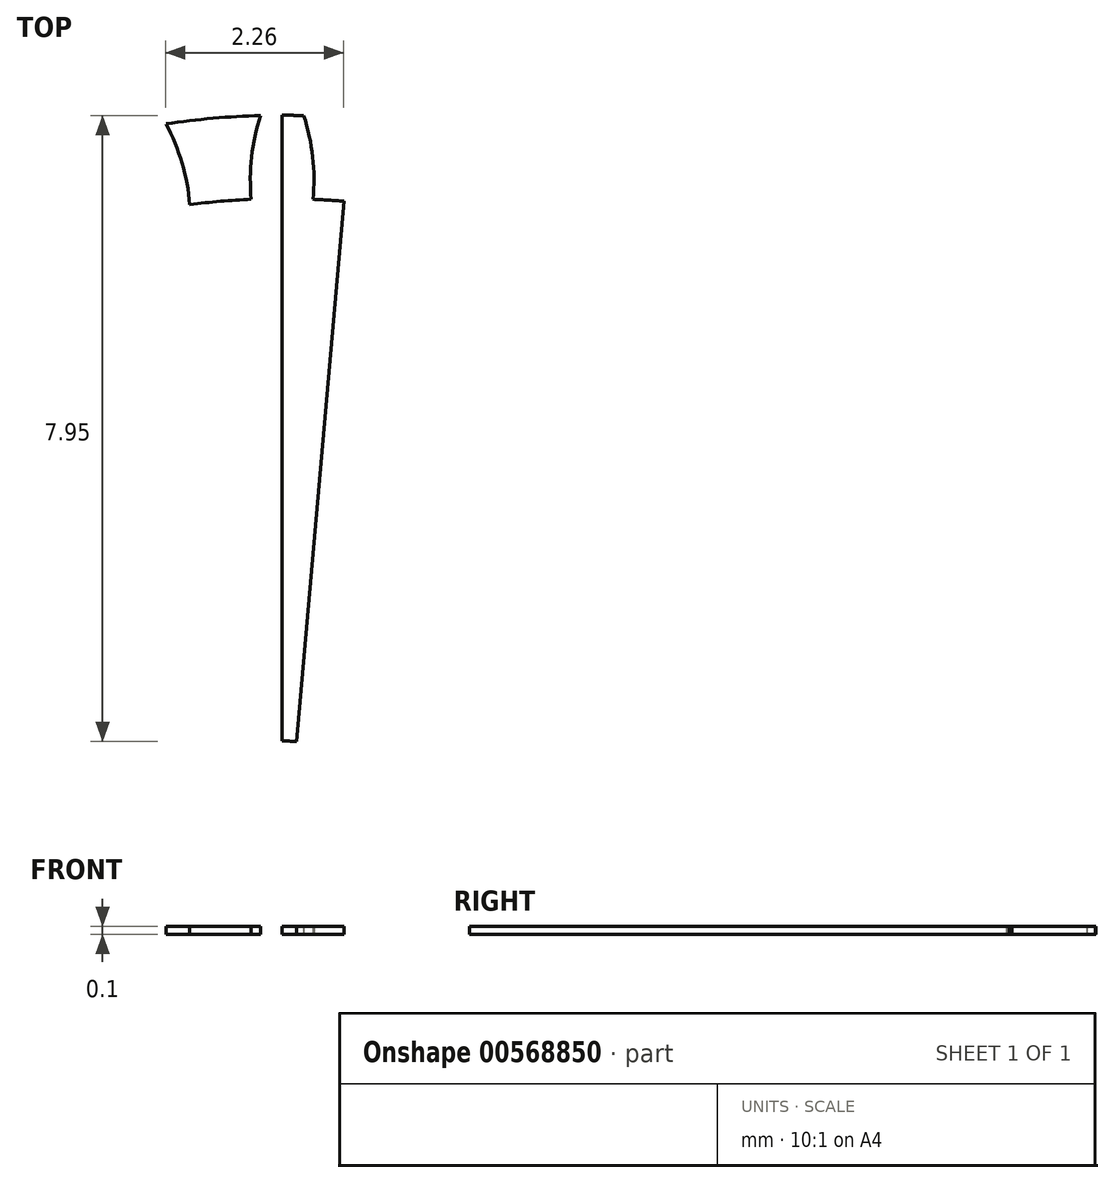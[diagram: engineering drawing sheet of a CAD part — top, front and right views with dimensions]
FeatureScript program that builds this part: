
annotation { "Feature Type Name" : "Feature", "Feature Type Description" : "" }
export const myFeature = defineFeature(function(context is Context, id is Id, definition is map)
    precondition{}
    {
        {
            var Q0;
            Q0=qCreatedBy(makeId("Top.planeOp"),FACE);
            var sketch = newSketch(context, id + "F0", { "sketchPlane" : qUnion([Q0])});
            skCircle(sketch, "E0", {"center": v(0, 0) * mm, "radius": 1.9 * mm});
            skCircle(sketch, "E1.0", {"center": v(0, 0) * mm, "radius": 2.1 * mm});
            skCircle(sketch, "E2", {"center": v(0, 0) * mm, "radius": 10.05 * mm});
            skLineSegment(sketch, "E3", {"start": v(0, 0) * mm, "end": v(0, 10.05) * mm});
            skLineSegment(sketch, "E4", {"start": v(0, 0) * mm, "end": v(0.88, 10.02) * mm});
            skPoint(sketch, "E5", {"position": v(0.27, 10.05) * mm});
            skPoint(sketch, "E6", {"position": v(0.39, 9.52) * mm});
            skPoint(sketch, "E7", {"position": v(0.4, 8.99) * mm});
            skArc(sketch, "E8", {"start": v(0.78, 8.96) * mm, "mid": v(0.59, 8.98) * mm, "end": v(0.4, 8.99) * mm});
            skArc(sketch, "E9", {"start": v(0, 10.05) * mm, "mid": v(0.14, 10.05) * mm, "end": v(0.27, 10.05) * mm});
            skArc(sketch, "E10", {"start": v(0.4, 8.99) * mm, "mid": v(0.39, 9.53) * mm, "end": v(0.27, 10.05) * mm});
            skArc(sketch, "E11.MirrorCS", {"start": v(-0.4, 8.99) * mm, "mid": v(-0.39, 9.53) * mm, "end": v(-0.27, 10.05) * mm});
            skArc(sketch, "E12.MirrorCS", {"start": v(0, 10.05) * mm, "mid": v(-0.14, 10.05) * mm, "end": v(-0.27, 10.05) * mm});
            skPoint(sketch, "E13.MirrorP", {"position": v(-0.4, 8.99) * mm});
            skArc(sketch, "E14.MirrorCS", {"start": v(-0.78, 8.96) * mm, "mid": v(-0.59, 8.98) * mm, "end": v(-0.4, 8.99) * mm});
            skPoint(sketch, "E15.MirrorP", {"position": v(-0.39, 9.52) * mm});
            skPoint(sketch, "E16.MirrorP", {"position": v(-0.27, 10.05) * mm});
            skPoint(sketch, "E17.1.0", {"position": v(-2.02, 9.85) * mm});
            skPoint(sketch, "E17.1.1", {"position": v(-1.95, 8.78) * mm});
            skPoint(sketch, "E17.1.2", {"position": v(-1.27, 9.44) * mm});
            skPoint(sketch, "E17.1.3", {"position": v(-2.04, 9.3) * mm});
            skPoint(sketch, "E17.1.4", {"position": v(-1.48, 9.95) * mm});
            skPoint(sketch, "E17.1.5", {"position": v(-1.17, 8.92) * mm});
            skArc(sketch, "E17.1.6", {"start": v(-1.17, 8.92) * mm, "mid": v(-1.27, 9.45) * mm, "end": v(-1.48, 9.95) * mm});
            skArc(sketch, "E17.1.7", {"start": v(-0.78, 8.96) * mm, "mid": v(-0.98, 8.94) * mm, "end": v(-1.17, 8.92) * mm});
            skArc(sketch, "E17.1.8", {"start": v(-1.95, 8.78) * mm, "mid": v(-2.04, 9.31) * mm, "end": v(-2.02, 9.85) * mm});
            skArc(sketch, "E17.1.9", {"start": v(-2.33, 8.69) * mm, "mid": v(-2.14, 8.74) * mm, "end": v(-1.95, 8.78) * mm});
            skArc(sketch, "E17.1.10", {"start": v(-1.75, 9.9) * mm, "mid": v(-1.61, 9.92) * mm, "end": v(-1.48, 9.95) * mm});
            skArc(sketch, "E17.1.11", {"start": v(-1.75, 9.9) * mm, "mid": v(-1.88, 9.88) * mm, "end": v(-2.02, 9.85) * mm});
            skPoint(sketch, "E17.2.0", {"position": v(-3.7, 9.35) * mm});
            skPoint(sketch, "E17.2.1", {"position": v(-3.44, 8.31) * mm});
            skPoint(sketch, "E17.2.2", {"position": v(-2.89, 9.08) * mm});
            skPoint(sketch, "E17.2.3", {"position": v(-3.62, 8.8) * mm});
            skPoint(sketch, "E17.2.4", {"position": v(-3.18, 9.54) * mm});
            skPoint(sketch, "E17.2.5", {"position": v(-2.7, 8.58) * mm});
            skArc(sketch, "E17.2.6", {"start": v(-2.7, 8.58) * mm, "mid": v(-2.9, 9.08) * mm, "end": v(-3.18, 9.54) * mm});
            skArc(sketch, "E17.2.7", {"start": v(-2.33, 8.69) * mm, "mid": v(-2.52, 8.64) * mm, "end": v(-2.7, 8.58) * mm});
            skArc(sketch, "E17.2.8", {"start": v(-3.44, 8.31) * mm, "mid": v(-3.62, 8.82) * mm, "end": v(-3.7, 9.35) * mm});
            skArc(sketch, "E17.2.9", {"start": v(-3.8, 8.15) * mm, "mid": v(-3.62, 8.23) * mm, "end": v(-3.44, 8.31) * mm});
            skArc(sketch, "E17.2.10", {"start": v(-3.44, 9.45) * mm, "mid": v(-3.3, 9.5) * mm, "end": v(-3.18, 9.54) * mm});
            skArc(sketch, "E17.2.11", {"start": v(-3.44, 9.45) * mm, "mid": v(-3.57, 9.4) * mm, "end": v(-3.7, 9.35) * mm});
            skPoint(sketch, "E17.3.0", {"position": v(-5.26, 8.57) * mm});
            skPoint(sketch, "E17.3.1", {"position": v(-4.83, 7.59) * mm});
            skPoint(sketch, "E17.3.2", {"position": v(-4.42, 8.44) * mm});
            skPoint(sketch, "E17.3.3", {"position": v(-5.1, 8.05) * mm});
            skPoint(sketch, "E17.3.4", {"position": v(-4.79, 8.84) * mm});
            skPoint(sketch, "E17.3.5", {"position": v(-4.15, 7.98) * mm});
            skArc(sketch, "E17.3.6", {"start": v(-4.15, 7.98) * mm, "mid": v(-4.43, 8.44) * mm, "end": v(-4.79, 8.84) * mm});
            skArc(sketch, "E17.3.7", {"start": v(-3.8, 8.15) * mm, "mid": v(-3.98, 8.07) * mm, "end": v(-4.15, 7.98) * mm});
            skArc(sketch, "E17.3.8", {"start": v(-4.83, 7.59) * mm, "mid": v(-5.1, 8.05) * mm, "end": v(-5.26, 8.57) * mm});
            skArc(sketch, "E17.3.9", {"start": v(-5.16, 7.37) * mm, "mid": v(-5, 7.48) * mm, "end": v(-4.83, 7.59) * mm});
            skArc(sketch, "E17.3.10", {"start": v(-5.03, 8.7) * mm, "mid": v(-4.9, 8.77) * mm, "end": v(-4.79, 8.84) * mm});
            skArc(sketch, "E17.3.11", {"start": v(-5.03, 8.7) * mm, "mid": v(-5.15, 8.64) * mm, "end": v(-5.26, 8.57) * mm});
            skPoint(sketch, "E17.4.0", {"position": v(-6.67, 7.52) * mm});
            skPoint(sketch, "E17.4.1", {"position": v(-6.08, 6.63) * mm});
            skPoint(sketch, "E17.4.2", {"position": v(-5.82, 7.54) * mm});
            skPoint(sketch, "E17.4.3", {"position": v(-6.42, 7.04) * mm});
            skPoint(sketch, "E17.4.4", {"position": v(-6.25, 7.88) * mm});
            skPoint(sketch, "E17.4.5", {"position": v(-5.48, 7.14) * mm});
            skArc(sketch, "E17.4.6", {"start": v(-5.48, 7.14) * mm, "mid": v(-5.82, 7.55) * mm, "end": v(-6.25, 7.88) * mm});
            skArc(sketch, "E17.4.7", {"start": v(-5.16, 7.37) * mm, "mid": v(-5.32, 7.25) * mm, "end": v(-5.48, 7.14) * mm});
            skArc(sketch, "E17.4.8", {"start": v(-6.08, 6.63) * mm, "mid": v(-6.42, 7.05) * mm, "end": v(-6.67, 7.52) * mm});
            skArc(sketch, "E17.4.9", {"start": v(-6.36, 6.36) * mm, "mid": v(-6.22, 6.5) * mm, "end": v(-6.08, 6.63) * mm});
            skArc(sketch, "E17.4.10", {"start": v(-6.46, 7.7) * mm, "mid": v(-6.36, 7.79) * mm, "end": v(-6.25, 7.88) * mm});
            skArc(sketch, "E17.4.11", {"start": v(-6.46, 7.7) * mm, "mid": v(-6.57, 7.61) * mm, "end": v(-6.67, 7.52) * mm});
            skPoint(sketch, "E17.5.0", {"position": v(-7.88, 6.25) * mm});
            skPoint(sketch, "E17.5.1", {"position": v(-7.14, 5.48) * mm});
            skPoint(sketch, "E17.5.2", {"position": v(-7.04, 6.42) * mm});
            skPoint(sketch, "E17.5.3", {"position": v(-7.54, 5.82) * mm});
            skPoint(sketch, "E17.5.4", {"position": v(-7.52, 6.67) * mm});
            skPoint(sketch, "E17.5.5", {"position": v(-6.63, 6.08) * mm});
            skArc(sketch, "E17.5.6", {"start": v(-6.63, 6.08) * mm, "mid": v(-7.05, 6.42) * mm, "end": v(-7.52, 6.67) * mm});
            skArc(sketch, "E17.5.7", {"start": v(-6.36, 6.36) * mm, "mid": v(-6.5, 6.22) * mm, "end": v(-6.63, 6.08) * mm});
            skArc(sketch, "E17.5.8", {"start": v(-7.14, 5.48) * mm, "mid": v(-7.55, 5.82) * mm, "end": v(-7.88, 6.25) * mm});
            skArc(sketch, "E17.5.9", {"start": v(-7.37, 5.16) * mm, "mid": v(-7.25, 5.32) * mm, "end": v(-7.14, 5.48) * mm});
            skArc(sketch, "E17.5.10", {"start": v(-7.7, 6.46) * mm, "mid": v(-7.61, 6.57) * mm, "end": v(-7.52, 6.67) * mm});
            skArc(sketch, "E17.5.11", {"start": v(-7.7, 6.46) * mm, "mid": v(-7.79, 6.36) * mm, "end": v(-7.88, 6.25) * mm});
            skPoint(sketch, "E17.6.0", {"position": v(-8.84, 4.79) * mm});
            skPoint(sketch, "E17.6.1", {"position": v(-7.98, 4.15) * mm});
            skPoint(sketch, "E17.6.2", {"position": v(-8.05, 5.1) * mm});
            skPoint(sketch, "E17.6.3", {"position": v(-8.44, 4.42) * mm});
            skPoint(sketch, "E17.6.4", {"position": v(-8.57, 5.26) * mm});
            skPoint(sketch, "E17.6.5", {"position": v(-7.59, 4.83) * mm});
            skArc(sketch, "E17.6.6", {"start": v(-7.59, 4.83) * mm, "mid": v(-8.05, 5.1) * mm, "end": v(-8.57, 5.26) * mm});
            skArc(sketch, "E17.6.7", {"start": v(-7.37, 5.16) * mm, "mid": v(-7.48, 5) * mm, "end": v(-7.59, 4.83) * mm});
            skArc(sketch, "E17.6.8", {"start": v(-7.98, 4.15) * mm, "mid": v(-8.44, 4.43) * mm, "end": v(-8.84, 4.79) * mm});
            skArc(sketch, "E17.6.9", {"start": v(-8.15, 3.8) * mm, "mid": v(-8.07, 3.98) * mm, "end": v(-7.98, 4.15) * mm});
            skArc(sketch, "E17.6.10", {"start": v(-8.7, 5.03) * mm, "mid": v(-8.64, 5.15) * mm, "end": v(-8.57, 5.26) * mm});
            skArc(sketch, "E17.6.11", {"start": v(-8.7, 5.03) * mm, "mid": v(-8.77, 4.9) * mm, "end": v(-8.84, 4.79) * mm});
            skPoint(sketch, "E17.7.0", {"position": v(-9.54, 3.18) * mm});
            skPoint(sketch, "E17.7.1", {"position": v(-8.58, 2.7) * mm});
            skPoint(sketch, "E17.7.2", {"position": v(-8.8, 3.62) * mm});
            skPoint(sketch, "E17.7.3", {"position": v(-9.08, 2.89) * mm});
            skPoint(sketch, "E17.7.4", {"position": v(-9.35, 3.7) * mm});
            skPoint(sketch, "E17.7.5", {"position": v(-8.31, 3.44) * mm});
            skArc(sketch, "E17.7.6", {"start": v(-8.31, 3.44) * mm, "mid": v(-8.82, 3.62) * mm, "end": v(-9.35, 3.7) * mm});
            skArc(sketch, "E17.7.7", {"start": v(-8.15, 3.8) * mm, "mid": v(-8.23, 3.62) * mm, "end": v(-8.31, 3.44) * mm});
            skArc(sketch, "E17.7.8", {"start": v(-8.58, 2.7) * mm, "mid": v(-9.08, 2.9) * mm, "end": v(-9.54, 3.18) * mm});
            skArc(sketch, "E17.7.9", {"start": v(-8.69, 2.33) * mm, "mid": v(-8.64, 2.52) * mm, "end": v(-8.58, 2.7) * mm});
            skArc(sketch, "E17.7.10", {"start": v(-9.45, 3.44) * mm, "mid": v(-9.4, 3.57) * mm, "end": v(-9.35, 3.7) * mm});
            skArc(sketch, "E17.7.11", {"start": v(-9.45, 3.44) * mm, "mid": v(-9.5, 3.3) * mm, "end": v(-9.54, 3.18) * mm});
            skPoint(sketch, "E17.8.0", {"position": v(-9.95, 1.48) * mm});
            skPoint(sketch, "E17.8.1", {"position": v(-8.92, 1.17) * mm});
            skPoint(sketch, "E17.8.2", {"position": v(-9.3, 2.04) * mm});
            skPoint(sketch, "E17.8.3", {"position": v(-9.44, 1.27) * mm});
            skPoint(sketch, "E17.8.4", {"position": v(-9.85, 2.02) * mm});
            skPoint(sketch, "E17.8.5", {"position": v(-8.78, 1.95) * mm});
            skArc(sketch, "E17.8.6", {"start": v(-8.78, 1.95) * mm, "mid": v(-9.31, 2.04) * mm, "end": v(-9.85, 2.02) * mm});
            skArc(sketch, "E17.8.7", {"start": v(-8.69, 2.33) * mm, "mid": v(-8.74, 2.14) * mm, "end": v(-8.78, 1.95) * mm});
            skArc(sketch, "E17.8.8", {"start": v(-8.92, 1.17) * mm, "mid": v(-9.45, 1.27) * mm, "end": v(-9.95, 1.48) * mm});
            skArc(sketch, "E17.8.9", {"start": v(-8.96, 0.78) * mm, "mid": v(-8.94, 0.98) * mm, "end": v(-8.92, 1.17) * mm});
            skArc(sketch, "E17.8.10", {"start": v(-9.9, 1.75) * mm, "mid": v(-9.88, 1.88) * mm, "end": v(-9.85, 2.02) * mm});
            skArc(sketch, "E17.8.11", {"start": v(-9.9, 1.75) * mm, "mid": v(-9.92, 1.61) * mm, "end": v(-9.95, 1.48) * mm});
            skPoint(sketch, "E17.9.0", {"position": v(-10.05, -0.27) * mm});
            skPoint(sketch, "E17.9.1", {"position": v(-8.99, -0.4) * mm});
            skPoint(sketch, "E17.9.2", {"position": v(-9.52, 0.39) * mm});
            skPoint(sketch, "E17.9.3", {"position": v(-9.52, -0.39) * mm});
            skPoint(sketch, "E17.9.4", {"position": v(-10.05, 0.27) * mm});
            skPoint(sketch, "E17.9.5", {"position": v(-8.99, 0.4) * mm});
            skArc(sketch, "E17.9.6", {"start": v(-8.99, 0.4) * mm, "mid": v(-9.53, 0.39) * mm, "end": v(-10.05, 0.27) * mm});
            skArc(sketch, "E17.9.7", {"start": v(-8.96, 0.78) * mm, "mid": v(-8.98, 0.59) * mm, "end": v(-8.99, 0.4) * mm});
            skArc(sketch, "E17.9.8", {"start": v(-8.99, -0.4) * mm, "mid": v(-9.53, -0.39) * mm, "end": v(-10.05, -0.27) * mm});
            skArc(sketch, "E17.9.9", {"start": v(-8.96, -0.78) * mm, "mid": v(-8.98, -0.59) * mm, "end": v(-8.99, -0.4) * mm});
            skArc(sketch, "E17.9.10", {"start": v(-10.05, 0) * mm, "mid": v(-10.05, 0.14) * mm, "end": v(-10.05, 0.27) * mm});
            skArc(sketch, "E17.9.11", {"start": v(-10.05, 0) * mm, "mid": v(-10.05, -0.14) * mm, "end": v(-10.05, -0.27) * mm});
            skPoint(sketch, "E17.10.0", {"position": v(-9.85, -2.02) * mm});
            skPoint(sketch, "E17.10.1", {"position": v(-8.78, -1.95) * mm});
            skPoint(sketch, "E17.10.2", {"position": v(-9.44, -1.27) * mm});
            skPoint(sketch, "E17.10.3", {"position": v(-9.3, -2.04) * mm});
            skPoint(sketch, "E17.10.4", {"position": v(-9.95, -1.48) * mm});
            skPoint(sketch, "E17.10.5", {"position": v(-8.92, -1.17) * mm});
            skArc(sketch, "E17.10.6", {"start": v(-8.92, -1.17) * mm, "mid": v(-9.45, -1.27) * mm, "end": v(-9.95, -1.48) * mm});
            skArc(sketch, "E17.10.7", {"start": v(-8.96, -0.78) * mm, "mid": v(-8.94, -0.98) * mm, "end": v(-8.92, -1.17) * mm});
            skArc(sketch, "E17.10.8", {"start": v(-8.78, -1.95) * mm, "mid": v(-9.31, -2.04) * mm, "end": v(-9.85, -2.02) * mm});
            skArc(sketch, "E17.10.9", {"start": v(-8.69, -2.33) * mm, "mid": v(-8.74, -2.14) * mm, "end": v(-8.78, -1.95) * mm});
            skArc(sketch, "E17.10.10", {"start": v(-9.9, -1.75) * mm, "mid": v(-9.92, -1.61) * mm, "end": v(-9.95, -1.48) * mm});
            skArc(sketch, "E17.10.11", {"start": v(-9.9, -1.75) * mm, "mid": v(-9.88, -1.88) * mm, "end": v(-9.85, -2.02) * mm});
            skPoint(sketch, "E17.11.0", {"position": v(-9.35, -3.7) * mm});
            skPoint(sketch, "E17.11.1", {"position": v(-8.31, -3.44) * mm});
            skPoint(sketch, "E17.11.2", {"position": v(-9.08, -2.89) * mm});
            skPoint(sketch, "E17.11.3", {"position": v(-8.8, -3.62) * mm});
            skPoint(sketch, "E17.11.4", {"position": v(-9.54, -3.18) * mm});
            skPoint(sketch, "E17.11.5", {"position": v(-8.58, -2.7) * mm});
            skArc(sketch, "E17.11.6", {"start": v(-8.58, -2.7) * mm, "mid": v(-9.08, -2.9) * mm, "end": v(-9.54, -3.18) * mm});
            skArc(sketch, "E17.11.7", {"start": v(-8.69, -2.33) * mm, "mid": v(-8.64, -2.52) * mm, "end": v(-8.58, -2.7) * mm});
            skArc(sketch, "E17.11.8", {"start": v(-8.31, -3.44) * mm, "mid": v(-8.82, -3.62) * mm, "end": v(-9.35, -3.7) * mm});
            skArc(sketch, "E17.11.9", {"start": v(-8.15, -3.8) * mm, "mid": v(-8.23, -3.62) * mm, "end": v(-8.31, -3.44) * mm});
            skArc(sketch, "E17.11.10", {"start": v(-9.45, -3.44) * mm, "mid": v(-9.5, -3.3) * mm, "end": v(-9.54, -3.18) * mm});
            skArc(sketch, "E17.11.11", {"start": v(-9.45, -3.44) * mm, "mid": v(-9.4, -3.57) * mm, "end": v(-9.35, -3.7) * mm});
            skPoint(sketch, "E17.12.0", {"position": v(-8.57, -5.26) * mm});
            skPoint(sketch, "E17.12.1", {"position": v(-7.59, -4.83) * mm});
            skPoint(sketch, "E17.12.2", {"position": v(-8.44, -4.42) * mm});
            skPoint(sketch, "E17.12.3", {"position": v(-8.05, -5.1) * mm});
            skPoint(sketch, "E17.12.4", {"position": v(-8.84, -4.79) * mm});
            skPoint(sketch, "E17.12.5", {"position": v(-7.98, -4.15) * mm});
            skArc(sketch, "E17.12.6", {"start": v(-7.98, -4.15) * mm, "mid": v(-8.44, -4.43) * mm, "end": v(-8.84, -4.79) * mm});
            skArc(sketch, "E17.12.7", {"start": v(-8.15, -3.8) * mm, "mid": v(-8.07, -3.98) * mm, "end": v(-7.98, -4.15) * mm});
            skArc(sketch, "E17.12.8", {"start": v(-7.59, -4.83) * mm, "mid": v(-8.05, -5.1) * mm, "end": v(-8.57, -5.26) * mm});
            skArc(sketch, "E17.12.9", {"start": v(-7.37, -5.16) * mm, "mid": v(-7.48, -5) * mm, "end": v(-7.59, -4.83) * mm});
            skArc(sketch, "E17.12.10", {"start": v(-8.7, -5.03) * mm, "mid": v(-8.77, -4.9) * mm, "end": v(-8.84, -4.79) * mm});
            skArc(sketch, "E17.12.11", {"start": v(-8.7, -5.03) * mm, "mid": v(-8.64, -5.15) * mm, "end": v(-8.57, -5.26) * mm});
            skPoint(sketch, "E17.13.0", {"position": v(-7.52, -6.67) * mm});
            skPoint(sketch, "E17.13.1", {"position": v(-6.63, -6.08) * mm});
            skPoint(sketch, "E17.13.2", {"position": v(-7.54, -5.82) * mm});
            skPoint(sketch, "E17.13.3", {"position": v(-7.04, -6.42) * mm});
            skPoint(sketch, "E17.13.4", {"position": v(-7.88, -6.25) * mm});
            skPoint(sketch, "E17.13.5", {"position": v(-7.14, -5.48) * mm});
            skArc(sketch, "E17.13.6", {"start": v(-7.14, -5.48) * mm, "mid": v(-7.55, -5.82) * mm, "end": v(-7.88, -6.25) * mm});
            skArc(sketch, "E17.13.7", {"start": v(-7.37, -5.16) * mm, "mid": v(-7.25, -5.32) * mm, "end": v(-7.14, -5.48) * mm});
            skArc(sketch, "E17.13.8", {"start": v(-6.63, -6.08) * mm, "mid": v(-7.05, -6.42) * mm, "end": v(-7.52, -6.67) * mm});
            skArc(sketch, "E17.13.9", {"start": v(-6.36, -6.36) * mm, "mid": v(-6.5, -6.22) * mm, "end": v(-6.63, -6.08) * mm});
            skArc(sketch, "E17.13.10", {"start": v(-7.7, -6.46) * mm, "mid": v(-7.79, -6.36) * mm, "end": v(-7.88, -6.25) * mm});
            skArc(sketch, "E17.13.11", {"start": v(-7.7, -6.46) * mm, "mid": v(-7.61, -6.57) * mm, "end": v(-7.52, -6.67) * mm});
            skPoint(sketch, "E17.14.0", {"position": v(-6.25, -7.88) * mm});
            skPoint(sketch, "E17.14.1", {"position": v(-5.48, -7.14) * mm});
            skPoint(sketch, "E17.14.2", {"position": v(-6.42, -7.04) * mm});
            skPoint(sketch, "E17.14.3", {"position": v(-5.82, -7.54) * mm});
            skPoint(sketch, "E17.14.4", {"position": v(-6.67, -7.52) * mm});
            skPoint(sketch, "E17.14.5", {"position": v(-6.08, -6.63) * mm});
            skArc(sketch, "E17.14.6", {"start": v(-6.08, -6.63) * mm, "mid": v(-6.42, -7.05) * mm, "end": v(-6.67, -7.52) * mm});
            skArc(sketch, "E17.14.7", {"start": v(-6.36, -6.36) * mm, "mid": v(-6.22, -6.5) * mm, "end": v(-6.08, -6.63) * mm});
            skArc(sketch, "E17.14.8", {"start": v(-5.48, -7.14) * mm, "mid": v(-5.82, -7.55) * mm, "end": v(-6.25, -7.88) * mm});
            skArc(sketch, "E17.14.9", {"start": v(-5.16, -7.37) * mm, "mid": v(-5.32, -7.25) * mm, "end": v(-5.48, -7.14) * mm});
            skArc(sketch, "E17.14.10", {"start": v(-6.46, -7.7) * mm, "mid": v(-6.57, -7.61) * mm, "end": v(-6.67, -7.52) * mm});
            skArc(sketch, "E17.14.11", {"start": v(-6.46, -7.7) * mm, "mid": v(-6.36, -7.79) * mm, "end": v(-6.25, -7.88) * mm});
            skPoint(sketch, "E17.15.0", {"position": v(-4.79, -8.84) * mm});
            skPoint(sketch, "E17.15.1", {"position": v(-4.15, -7.98) * mm});
            skPoint(sketch, "E17.15.2", {"position": v(-5.1, -8.05) * mm});
            skPoint(sketch, "E17.15.3", {"position": v(-4.42, -8.44) * mm});
            skPoint(sketch, "E17.15.4", {"position": v(-5.26, -8.57) * mm});
            skPoint(sketch, "E17.15.5", {"position": v(-4.83, -7.59) * mm});
            skArc(sketch, "E17.15.6", {"start": v(-4.83, -7.59) * mm, "mid": v(-5.1, -8.05) * mm, "end": v(-5.26, -8.57) * mm});
            skArc(sketch, "E17.15.7", {"start": v(-5.16, -7.37) * mm, "mid": v(-5, -7.48) * mm, "end": v(-4.83, -7.59) * mm});
            skArc(sketch, "E17.15.8", {"start": v(-4.15, -7.98) * mm, "mid": v(-4.43, -8.44) * mm, "end": v(-4.79, -8.84) * mm});
            skArc(sketch, "E17.15.9", {"start": v(-3.8, -8.15) * mm, "mid": v(-3.98, -8.07) * mm, "end": v(-4.15, -7.98) * mm});
            skArc(sketch, "E17.15.10", {"start": v(-5.03, -8.7) * mm, "mid": v(-5.15, -8.64) * mm, "end": v(-5.26, -8.57) * mm});
            skArc(sketch, "E17.15.11", {"start": v(-5.03, -8.7) * mm, "mid": v(-4.9, -8.77) * mm, "end": v(-4.79, -8.84) * mm});
            skPoint(sketch, "E17.16.0", {"position": v(-3.18, -9.54) * mm});
            skPoint(sketch, "E17.16.1", {"position": v(-2.7, -8.58) * mm});
            skPoint(sketch, "E17.16.2", {"position": v(-3.62, -8.8) * mm});
            skPoint(sketch, "E17.16.3", {"position": v(-2.89, -9.08) * mm});
            skPoint(sketch, "E17.16.4", {"position": v(-3.7, -9.35) * mm});
            skPoint(sketch, "E17.16.5", {"position": v(-3.44, -8.31) * mm});
            skArc(sketch, "E17.16.6", {"start": v(-3.44, -8.31) * mm, "mid": v(-3.62, -8.82) * mm, "end": v(-3.7, -9.35) * mm});
            skArc(sketch, "E17.16.7", {"start": v(-3.8, -8.15) * mm, "mid": v(-3.62, -8.23) * mm, "end": v(-3.44, -8.31) * mm});
            skArc(sketch, "E17.16.8", {"start": v(-2.7, -8.58) * mm, "mid": v(-2.9, -9.08) * mm, "end": v(-3.18, -9.54) * mm});
            skArc(sketch, "E17.16.9", {"start": v(-2.33, -8.69) * mm, "mid": v(-2.52, -8.64) * mm, "end": v(-2.7, -8.58) * mm});
            skArc(sketch, "E17.16.10", {"start": v(-3.44, -9.45) * mm, "mid": v(-3.57, -9.4) * mm, "end": v(-3.7, -9.35) * mm});
            skArc(sketch, "E17.16.11", {"start": v(-3.44, -9.45) * mm, "mid": v(-3.3, -9.5) * mm, "end": v(-3.18, -9.54) * mm});
            skPoint(sketch, "E17.17.0", {"position": v(-1.48, -9.95) * mm});
            skPoint(sketch, "E17.17.1", {"position": v(-1.17, -8.92) * mm});
            skPoint(sketch, "E17.17.2", {"position": v(-2.04, -9.3) * mm});
            skPoint(sketch, "E17.17.3", {"position": v(-1.27, -9.44) * mm});
            skPoint(sketch, "E17.17.4", {"position": v(-2.02, -9.85) * mm});
            skPoint(sketch, "E17.17.5", {"position": v(-1.95, -8.78) * mm});
            skArc(sketch, "E17.17.6", {"start": v(-1.95, -8.78) * mm, "mid": v(-2.04, -9.31) * mm, "end": v(-2.02, -9.85) * mm});
            skArc(sketch, "E17.17.7", {"start": v(-2.33, -8.69) * mm, "mid": v(-2.14, -8.74) * mm, "end": v(-1.95, -8.78) * mm});
            skArc(sketch, "E17.17.8", {"start": v(-1.17, -8.92) * mm, "mid": v(-1.27, -9.45) * mm, "end": v(-1.48, -9.95) * mm});
            skArc(sketch, "E17.17.9", {"start": v(-0.78, -8.96) * mm, "mid": v(-0.98, -8.94) * mm, "end": v(-1.17, -8.92) * mm});
            skArc(sketch, "E17.17.10", {"start": v(-1.75, -9.9) * mm, "mid": v(-1.88, -9.88) * mm, "end": v(-2.02, -9.85) * mm});
            skArc(sketch, "E17.17.11", {"start": v(-1.75, -9.9) * mm, "mid": v(-1.61, -9.92) * mm, "end": v(-1.48, -9.95) * mm});
            skPoint(sketch, "E17.18.0", {"position": v(0.27, -10.05) * mm});
            skPoint(sketch, "E17.18.1", {"position": v(0.4, -8.99) * mm});
            skPoint(sketch, "E17.18.2", {"position": v(-0.39, -9.52) * mm});
            skPoint(sketch, "E17.18.3", {"position": v(0.39, -9.52) * mm});
            skPoint(sketch, "E17.18.4", {"position": v(-0.27, -10.05) * mm});
            skPoint(sketch, "E17.18.5", {"position": v(-0.4, -8.99) * mm});
            skArc(sketch, "E17.18.6", {"start": v(-0.4, -8.99) * mm, "mid": v(-0.39, -9.53) * mm, "end": v(-0.27, -10.05) * mm});
            skArc(sketch, "E17.18.7", {"start": v(-0.78, -8.96) * mm, "mid": v(-0.59, -8.98) * mm, "end": v(-0.4, -8.99) * mm});
            skArc(sketch, "E17.18.8", {"start": v(0.4, -8.99) * mm, "mid": v(0.39, -9.53) * mm, "end": v(0.27, -10.05) * mm});
            skArc(sketch, "E17.18.9", {"start": v(0.78, -8.96) * mm, "mid": v(0.59, -8.98) * mm, "end": v(0.4, -8.99) * mm});
            skArc(sketch, "E17.18.10", {"start": v(0, -10.05) * mm, "mid": v(-0.14, -10.05) * mm, "end": v(-0.27, -10.05) * mm});
            skArc(sketch, "E17.18.11", {"start": v(0, -10.05) * mm, "mid": v(0.14, -10.05) * mm, "end": v(0.27, -10.05) * mm});
            skPoint(sketch, "E17.19.0", {"position": v(2.02, -9.85) * mm});
            skPoint(sketch, "E17.19.1", {"position": v(1.95, -8.78) * mm});
            skPoint(sketch, "E17.19.2", {"position": v(1.27, -9.44) * mm});
            skPoint(sketch, "E17.19.3", {"position": v(2.04, -9.3) * mm});
            skPoint(sketch, "E17.19.4", {"position": v(1.48, -9.95) * mm});
            skPoint(sketch, "E17.19.5", {"position": v(1.17, -8.92) * mm});
            skArc(sketch, "E17.19.6", {"start": v(1.17, -8.92) * mm, "mid": v(1.27, -9.45) * mm, "end": v(1.48, -9.95) * mm});
            skArc(sketch, "E17.19.7", {"start": v(0.78, -8.96) * mm, "mid": v(0.98, -8.94) * mm, "end": v(1.17, -8.92) * mm});
            skArc(sketch, "E17.19.8", {"start": v(1.95, -8.78) * mm, "mid": v(2.04, -9.31) * mm, "end": v(2.02, -9.85) * mm});
            skArc(sketch, "E17.19.9", {"start": v(2.33, -8.69) * mm, "mid": v(2.14, -8.74) * mm, "end": v(1.95, -8.78) * mm});
            skArc(sketch, "E17.19.10", {"start": v(1.75, -9.9) * mm, "mid": v(1.61, -9.92) * mm, "end": v(1.48, -9.95) * mm});
            skArc(sketch, "E17.19.11", {"start": v(1.75, -9.9) * mm, "mid": v(1.88, -9.88) * mm, "end": v(2.02, -9.85) * mm});
            skPoint(sketch, "E17.20.0", {"position": v(3.7, -9.35) * mm});
            skPoint(sketch, "E17.20.1", {"position": v(3.44, -8.31) * mm});
            skPoint(sketch, "E17.20.2", {"position": v(2.89, -9.08) * mm});
            skPoint(sketch, "E17.20.3", {"position": v(3.62, -8.8) * mm});
            skPoint(sketch, "E17.20.4", {"position": v(3.18, -9.54) * mm});
            skPoint(sketch, "E17.20.5", {"position": v(2.7, -8.58) * mm});
            skArc(sketch, "E17.20.6", {"start": v(2.7, -8.58) * mm, "mid": v(2.9, -9.08) * mm, "end": v(3.18, -9.54) * mm});
            skArc(sketch, "E17.20.7", {"start": v(2.33, -8.69) * mm, "mid": v(2.52, -8.64) * mm, "end": v(2.7, -8.58) * mm});
            skArc(sketch, "E17.20.8", {"start": v(3.44, -8.31) * mm, "mid": v(3.62, -8.82) * mm, "end": v(3.7, -9.35) * mm});
            skArc(sketch, "E17.20.9", {"start": v(3.8, -8.15) * mm, "mid": v(3.62, -8.23) * mm, "end": v(3.44, -8.31) * mm});
            skArc(sketch, "E17.20.10", {"start": v(3.44, -9.45) * mm, "mid": v(3.3, -9.5) * mm, "end": v(3.18, -9.54) * mm});
            skArc(sketch, "E17.20.11", {"start": v(3.44, -9.45) * mm, "mid": v(3.57, -9.4) * mm, "end": v(3.7, -9.35) * mm});
            skPoint(sketch, "E17.21.0", {"position": v(5.26, -8.57) * mm});
            skPoint(sketch, "E17.21.1", {"position": v(4.83, -7.59) * mm});
            skPoint(sketch, "E17.21.2", {"position": v(4.42, -8.44) * mm});
            skPoint(sketch, "E17.21.3", {"position": v(5.1, -8.05) * mm});
            skPoint(sketch, "E17.21.4", {"position": v(4.79, -8.84) * mm});
            skPoint(sketch, "E17.21.5", {"position": v(4.15, -7.98) * mm});
            skArc(sketch, "E17.21.6", {"start": v(4.15, -7.98) * mm, "mid": v(4.43, -8.44) * mm, "end": v(4.79, -8.84) * mm});
            skArc(sketch, "E17.21.7", {"start": v(3.8, -8.15) * mm, "mid": v(3.98, -8.07) * mm, "end": v(4.15, -7.98) * mm});
            skArc(sketch, "E17.21.8", {"start": v(4.83, -7.59) * mm, "mid": v(5.1, -8.05) * mm, "end": v(5.26, -8.57) * mm});
            skArc(sketch, "E17.21.9", {"start": v(5.16, -7.37) * mm, "mid": v(5, -7.48) * mm, "end": v(4.83, -7.59) * mm});
            skArc(sketch, "E17.21.10", {"start": v(5.03, -8.7) * mm, "mid": v(4.9, -8.77) * mm, "end": v(4.79, -8.84) * mm});
            skArc(sketch, "E17.21.11", {"start": v(5.03, -8.7) * mm, "mid": v(5.15, -8.64) * mm, "end": v(5.26, -8.57) * mm});
            skPoint(sketch, "E17.22.0", {"position": v(6.67, -7.52) * mm});
            skPoint(sketch, "E17.22.1", {"position": v(6.08, -6.63) * mm});
            skPoint(sketch, "E17.22.2", {"position": v(5.82, -7.54) * mm});
            skPoint(sketch, "E17.22.3", {"position": v(6.42, -7.04) * mm});
            skPoint(sketch, "E17.22.4", {"position": v(6.25, -7.88) * mm});
            skPoint(sketch, "E17.22.5", {"position": v(5.48, -7.14) * mm});
            skArc(sketch, "E17.22.6", {"start": v(5.48, -7.14) * mm, "mid": v(5.82, -7.55) * mm, "end": v(6.25, -7.88) * mm});
            skArc(sketch, "E17.22.7", {"start": v(5.16, -7.37) * mm, "mid": v(5.32, -7.25) * mm, "end": v(5.48, -7.14) * mm});
            skArc(sketch, "E17.22.8", {"start": v(6.08, -6.63) * mm, "mid": v(6.42, -7.05) * mm, "end": v(6.67, -7.52) * mm});
            skArc(sketch, "E17.22.9", {"start": v(6.36, -6.36) * mm, "mid": v(6.22, -6.5) * mm, "end": v(6.08, -6.63) * mm});
            skArc(sketch, "E17.22.10", {"start": v(6.46, -7.7) * mm, "mid": v(6.36, -7.79) * mm, "end": v(6.25, -7.88) * mm});
            skArc(sketch, "E17.22.11", {"start": v(6.46, -7.7) * mm, "mid": v(6.57, -7.61) * mm, "end": v(6.67, -7.52) * mm});
            skPoint(sketch, "E17.23.0", {"position": v(7.88, -6.25) * mm});
            skPoint(sketch, "E17.23.1", {"position": v(7.14, -5.48) * mm});
            skPoint(sketch, "E17.23.2", {"position": v(7.04, -6.42) * mm});
            skPoint(sketch, "E17.23.3", {"position": v(7.54, -5.82) * mm});
            skPoint(sketch, "E17.23.4", {"position": v(7.52, -6.67) * mm});
            skPoint(sketch, "E17.23.5", {"position": v(6.63, -6.08) * mm});
            skArc(sketch, "E17.23.6", {"start": v(6.63, -6.08) * mm, "mid": v(7.05, -6.42) * mm, "end": v(7.52, -6.67) * mm});
            skArc(sketch, "E17.23.7", {"start": v(6.36, -6.36) * mm, "mid": v(6.5, -6.22) * mm, "end": v(6.63, -6.08) * mm});
            skArc(sketch, "E17.23.8", {"start": v(7.14, -5.48) * mm, "mid": v(7.55, -5.82) * mm, "end": v(7.88, -6.25) * mm});
            skArc(sketch, "E17.23.9", {"start": v(7.37, -5.16) * mm, "mid": v(7.25, -5.32) * mm, "end": v(7.14, -5.48) * mm});
            skArc(sketch, "E17.23.10", {"start": v(7.7, -6.46) * mm, "mid": v(7.61, -6.57) * mm, "end": v(7.52, -6.67) * mm});
            skArc(sketch, "E17.23.11", {"start": v(7.7, -6.46) * mm, "mid": v(7.79, -6.36) * mm, "end": v(7.88, -6.25) * mm});
            skPoint(sketch, "E17.24.0", {"position": v(8.84, -4.79) * mm});
            skPoint(sketch, "E17.24.1", {"position": v(7.98, -4.15) * mm});
            skPoint(sketch, "E17.24.2", {"position": v(8.05, -5.1) * mm});
            skPoint(sketch, "E17.24.3", {"position": v(8.44, -4.42) * mm});
            skPoint(sketch, "E17.24.4", {"position": v(8.57, -5.26) * mm});
            skPoint(sketch, "E17.24.5", {"position": v(7.59, -4.83) * mm});
            skArc(sketch, "E17.24.6", {"start": v(7.59, -4.83) * mm, "mid": v(8.05, -5.1) * mm, "end": v(8.57, -5.26) * mm});
            skArc(sketch, "E17.24.7", {"start": v(7.37, -5.16) * mm, "mid": v(7.48, -5) * mm, "end": v(7.59, -4.83) * mm});
            skArc(sketch, "E17.24.8", {"start": v(7.98, -4.15) * mm, "mid": v(8.44, -4.43) * mm, "end": v(8.84, -4.79) * mm});
            skArc(sketch, "E17.24.9", {"start": v(8.15, -3.8) * mm, "mid": v(8.07, -3.98) * mm, "end": v(7.98, -4.15) * mm});
            skArc(sketch, "E17.24.10", {"start": v(8.7, -5.03) * mm, "mid": v(8.64, -5.15) * mm, "end": v(8.57, -5.26) * mm});
            skArc(sketch, "E17.24.11", {"start": v(8.7, -5.03) * mm, "mid": v(8.77, -4.9) * mm, "end": v(8.84, -4.79) * mm});
            skPoint(sketch, "E17.25.0", {"position": v(9.54, -3.18) * mm});
            skPoint(sketch, "E17.25.1", {"position": v(8.58, -2.7) * mm});
            skPoint(sketch, "E17.25.2", {"position": v(8.8, -3.62) * mm});
            skPoint(sketch, "E17.25.3", {"position": v(9.08, -2.89) * mm});
            skPoint(sketch, "E17.25.4", {"position": v(9.35, -3.7) * mm});
            skPoint(sketch, "E17.25.5", {"position": v(8.31, -3.44) * mm});
            skArc(sketch, "E17.25.6", {"start": v(8.31, -3.44) * mm, "mid": v(8.82, -3.62) * mm, "end": v(9.35, -3.7) * mm});
            skArc(sketch, "E17.25.7", {"start": v(8.15, -3.8) * mm, "mid": v(8.23, -3.62) * mm, "end": v(8.31, -3.44) * mm});
            skArc(sketch, "E17.25.8", {"start": v(8.58, -2.7) * mm, "mid": v(9.08, -2.9) * mm, "end": v(9.54, -3.18) * mm});
            skArc(sketch, "E17.25.9", {"start": v(8.69, -2.33) * mm, "mid": v(8.64, -2.52) * mm, "end": v(8.58, -2.7) * mm});
            skArc(sketch, "E17.25.10", {"start": v(9.45, -3.44) * mm, "mid": v(9.4, -3.57) * mm, "end": v(9.35, -3.7) * mm});
            skArc(sketch, "E17.25.11", {"start": v(9.45, -3.44) * mm, "mid": v(9.5, -3.3) * mm, "end": v(9.54, -3.18) * mm});
            skPoint(sketch, "E17.26.0", {"position": v(9.95, -1.48) * mm});
            skPoint(sketch, "E17.26.1", {"position": v(8.92, -1.17) * mm});
            skPoint(sketch, "E17.26.2", {"position": v(9.3, -2.04) * mm});
            skPoint(sketch, "E17.26.3", {"position": v(9.44, -1.27) * mm});
            skPoint(sketch, "E17.26.4", {"position": v(9.85, -2.02) * mm});
            skPoint(sketch, "E17.26.5", {"position": v(8.78, -1.95) * mm});
            skArc(sketch, "E17.26.6", {"start": v(8.78, -1.95) * mm, "mid": v(9.31, -2.04) * mm, "end": v(9.85, -2.02) * mm});
            skArc(sketch, "E17.26.7", {"start": v(8.69, -2.33) * mm, "mid": v(8.74, -2.14) * mm, "end": v(8.78, -1.95) * mm});
            skArc(sketch, "E17.26.8", {"start": v(8.92, -1.17) * mm, "mid": v(9.45, -1.27) * mm, "end": v(9.95, -1.48) * mm});
            skArc(sketch, "E17.26.9", {"start": v(8.96, -0.78) * mm, "mid": v(8.94, -0.98) * mm, "end": v(8.92, -1.17) * mm});
            skArc(sketch, "E17.26.10", {"start": v(9.9, -1.75) * mm, "mid": v(9.88, -1.88) * mm, "end": v(9.85, -2.02) * mm});
            skArc(sketch, "E17.26.11", {"start": v(9.9, -1.75) * mm, "mid": v(9.92, -1.61) * mm, "end": v(9.95, -1.48) * mm});
            skPoint(sketch, "E17.27.0", {"position": v(10.05, 0.27) * mm});
            skPoint(sketch, "E17.27.1", {"position": v(8.99, 0.4) * mm});
            skPoint(sketch, "E17.27.2", {"position": v(9.52, -0.39) * mm});
            skPoint(sketch, "E17.27.3", {"position": v(9.52, 0.39) * mm});
            skPoint(sketch, "E17.27.4", {"position": v(10.05, -0.27) * mm});
            skPoint(sketch, "E17.27.5", {"position": v(8.99, -0.4) * mm});
            skArc(sketch, "E17.27.6", {"start": v(8.99, -0.4) * mm, "mid": v(9.53, -0.39) * mm, "end": v(10.05, -0.27) * mm});
            skArc(sketch, "E17.27.7", {"start": v(8.96, -0.78) * mm, "mid": v(8.98, -0.59) * mm, "end": v(8.99, -0.4) * mm});
            skArc(sketch, "E17.27.8", {"start": v(8.99, 0.4) * mm, "mid": v(9.53, 0.39) * mm, "end": v(10.05, 0.27) * mm});
            skArc(sketch, "E17.27.9", {"start": v(8.96, 0.78) * mm, "mid": v(8.98, 0.59) * mm, "end": v(8.99, 0.4) * mm});
            skArc(sketch, "E17.27.10", {"start": v(10.05, 0) * mm, "mid": v(10.05, -0.14) * mm, "end": v(10.05, -0.27) * mm});
            skArc(sketch, "E17.27.11", {"start": v(10.05, 0) * mm, "mid": v(10.05, 0.14) * mm, "end": v(10.05, 0.27) * mm});
            skPoint(sketch, "E17.28.0", {"position": v(9.85, 2.02) * mm});
            skPoint(sketch, "E17.28.1", {"position": v(8.78, 1.95) * mm});
            skPoint(sketch, "E17.28.2", {"position": v(9.44, 1.27) * mm});
            skPoint(sketch, "E17.28.3", {"position": v(9.3, 2.04) * mm});
            skPoint(sketch, "E17.28.4", {"position": v(9.95, 1.48) * mm});
            skPoint(sketch, "E17.28.5", {"position": v(8.92, 1.17) * mm});
            skArc(sketch, "E17.28.6", {"start": v(8.92, 1.17) * mm, "mid": v(9.45, 1.27) * mm, "end": v(9.95, 1.48) * mm});
            skArc(sketch, "E17.28.7", {"start": v(8.96, 0.78) * mm, "mid": v(8.94, 0.98) * mm, "end": v(8.92, 1.17) * mm});
            skArc(sketch, "E17.28.8", {"start": v(8.78, 1.95) * mm, "mid": v(9.31, 2.04) * mm, "end": v(9.85, 2.02) * mm});
            skArc(sketch, "E17.28.9", {"start": v(8.69, 2.33) * mm, "mid": v(8.74, 2.14) * mm, "end": v(8.78, 1.95) * mm});
            skArc(sketch, "E17.28.10", {"start": v(9.9, 1.75) * mm, "mid": v(9.92, 1.61) * mm, "end": v(9.95, 1.48) * mm});
            skArc(sketch, "E17.28.11", {"start": v(9.9, 1.75) * mm, "mid": v(9.88, 1.88) * mm, "end": v(9.85, 2.02) * mm});
            skPoint(sketch, "E17.29.0", {"position": v(9.35, 3.7) * mm});
            skPoint(sketch, "E17.29.1", {"position": v(8.31, 3.44) * mm});
            skPoint(sketch, "E17.29.2", {"position": v(9.08, 2.89) * mm});
            skPoint(sketch, "E17.29.3", {"position": v(8.8, 3.62) * mm});
            skPoint(sketch, "E17.29.4", {"position": v(9.54, 3.18) * mm});
            skPoint(sketch, "E17.29.5", {"position": v(8.58, 2.7) * mm});
            skArc(sketch, "E17.29.6", {"start": v(8.58, 2.7) * mm, "mid": v(9.08, 2.9) * mm, "end": v(9.54, 3.18) * mm});
            skArc(sketch, "E17.29.7", {"start": v(8.69, 2.33) * mm, "mid": v(8.64, 2.52) * mm, "end": v(8.58, 2.7) * mm});
            skArc(sketch, "E17.29.8", {"start": v(8.31, 3.44) * mm, "mid": v(8.82, 3.62) * mm, "end": v(9.35, 3.7) * mm});
            skArc(sketch, "E17.29.9", {"start": v(8.15, 3.8) * mm, "mid": v(8.23, 3.62) * mm, "end": v(8.31, 3.44) * mm});
            skArc(sketch, "E17.29.10", {"start": v(9.45, 3.44) * mm, "mid": v(9.5, 3.3) * mm, "end": v(9.54, 3.18) * mm});
            skArc(sketch, "E17.29.11", {"start": v(9.45, 3.44) * mm, "mid": v(9.4, 3.57) * mm, "end": v(9.35, 3.7) * mm});
            skPoint(sketch, "E17.30.0", {"position": v(8.57, 5.26) * mm});
            skPoint(sketch, "E17.30.1", {"position": v(7.59, 4.83) * mm});
            skPoint(sketch, "E17.30.2", {"position": v(8.44, 4.42) * mm});
            skPoint(sketch, "E17.30.3", {"position": v(8.05, 5.1) * mm});
            skPoint(sketch, "E17.30.4", {"position": v(8.84, 4.79) * mm});
            skPoint(sketch, "E17.30.5", {"position": v(7.98, 4.15) * mm});
            skArc(sketch, "E17.30.6", {"start": v(7.98, 4.15) * mm, "mid": v(8.44, 4.43) * mm, "end": v(8.84, 4.79) * mm});
            skArc(sketch, "E17.30.7", {"start": v(8.15, 3.8) * mm, "mid": v(8.07, 3.98) * mm, "end": v(7.98, 4.15) * mm});
            skArc(sketch, "E17.30.8", {"start": v(7.59, 4.83) * mm, "mid": v(8.05, 5.1) * mm, "end": v(8.57, 5.26) * mm});
            skArc(sketch, "E17.30.9", {"start": v(7.37, 5.16) * mm, "mid": v(7.48, 5) * mm, "end": v(7.59, 4.83) * mm});
            skArc(sketch, "E17.30.10", {"start": v(8.7, 5.03) * mm, "mid": v(8.77, 4.9) * mm, "end": v(8.84, 4.79) * mm});
            skArc(sketch, "E17.30.11", {"start": v(8.7, 5.03) * mm, "mid": v(8.64, 5.15) * mm, "end": v(8.57, 5.26) * mm});
            skPoint(sketch, "E17.31.0", {"position": v(7.52, 6.67) * mm});
            skPoint(sketch, "E17.31.1", {"position": v(6.63, 6.08) * mm});
            skPoint(sketch, "E17.31.2", {"position": v(7.54, 5.82) * mm});
            skPoint(sketch, "E17.31.3", {"position": v(7.04, 6.42) * mm});
            skPoint(sketch, "E17.31.4", {"position": v(7.88, 6.25) * mm});
            skPoint(sketch, "E17.31.5", {"position": v(7.14, 5.48) * mm});
            skArc(sketch, "E17.31.6", {"start": v(7.14, 5.48) * mm, "mid": v(7.55, 5.82) * mm, "end": v(7.88, 6.25) * mm});
            skArc(sketch, "E17.31.7", {"start": v(7.37, 5.16) * mm, "mid": v(7.25, 5.32) * mm, "end": v(7.14, 5.48) * mm});
            skArc(sketch, "E17.31.8", {"start": v(6.63, 6.08) * mm, "mid": v(7.05, 6.42) * mm, "end": v(7.52, 6.67) * mm});
            skArc(sketch, "E17.31.9", {"start": v(6.36, 6.36) * mm, "mid": v(6.5, 6.22) * mm, "end": v(6.63, 6.08) * mm});
            skArc(sketch, "E17.31.10", {"start": v(7.7, 6.46) * mm, "mid": v(7.79, 6.36) * mm, "end": v(7.88, 6.25) * mm});
            skArc(sketch, "E17.31.11", {"start": v(7.7, 6.46) * mm, "mid": v(7.61, 6.57) * mm, "end": v(7.52, 6.67) * mm});
            skPoint(sketch, "E17.32.0", {"position": v(6.25, 7.88) * mm});
            skPoint(sketch, "E17.32.1", {"position": v(5.48, 7.14) * mm});
            skPoint(sketch, "E17.32.2", {"position": v(6.42, 7.04) * mm});
            skPoint(sketch, "E17.32.3", {"position": v(5.82, 7.54) * mm});
            skPoint(sketch, "E17.32.4", {"position": v(6.67, 7.52) * mm});
            skPoint(sketch, "E17.32.5", {"position": v(6.08, 6.63) * mm});
            skArc(sketch, "E17.32.6", {"start": v(6.08, 6.63) * mm, "mid": v(6.42, 7.05) * mm, "end": v(6.67, 7.52) * mm});
            skArc(sketch, "E17.32.7", {"start": v(6.36, 6.36) * mm, "mid": v(6.22, 6.5) * mm, "end": v(6.08, 6.63) * mm});
            skArc(sketch, "E17.32.8", {"start": v(5.48, 7.14) * mm, "mid": v(5.82, 7.55) * mm, "end": v(6.25, 7.88) * mm});
            skArc(sketch, "E17.32.9", {"start": v(5.16, 7.37) * mm, "mid": v(5.32, 7.25) * mm, "end": v(5.48, 7.14) * mm});
            skArc(sketch, "E17.32.10", {"start": v(6.46, 7.7) * mm, "mid": v(6.57, 7.61) * mm, "end": v(6.67, 7.52) * mm});
            skArc(sketch, "E17.32.11", {"start": v(6.46, 7.7) * mm, "mid": v(6.36, 7.79) * mm, "end": v(6.25, 7.88) * mm});
            skPoint(sketch, "E17.33.0", {"position": v(4.79, 8.84) * mm});
            skPoint(sketch, "E17.33.1", {"position": v(4.15, 7.98) * mm});
            skPoint(sketch, "E17.33.2", {"position": v(5.1, 8.05) * mm});
            skPoint(sketch, "E17.33.3", {"position": v(4.42, 8.44) * mm});
            skPoint(sketch, "E17.33.4", {"position": v(5.26, 8.57) * mm});
            skPoint(sketch, "E17.33.5", {"position": v(4.83, 7.59) * mm});
            skArc(sketch, "E17.33.6", {"start": v(4.83, 7.59) * mm, "mid": v(5.1, 8.05) * mm, "end": v(5.26, 8.57) * mm});
            skArc(sketch, "E17.33.7", {"start": v(5.16, 7.37) * mm, "mid": v(5, 7.48) * mm, "end": v(4.83, 7.59) * mm});
            skArc(sketch, "E17.33.8", {"start": v(4.15, 7.98) * mm, "mid": v(4.43, 8.44) * mm, "end": v(4.79, 8.84) * mm});
            skArc(sketch, "E17.33.9", {"start": v(3.8, 8.15) * mm, "mid": v(3.98, 8.07) * mm, "end": v(4.15, 7.98) * mm});
            skArc(sketch, "E17.33.10", {"start": v(5.03, 8.7) * mm, "mid": v(5.15, 8.64) * mm, "end": v(5.26, 8.57) * mm});
            skArc(sketch, "E17.33.11", {"start": v(5.03, 8.7) * mm, "mid": v(4.9, 8.77) * mm, "end": v(4.79, 8.84) * mm});
            skPoint(sketch, "E17.34.0", {"position": v(3.18, 9.54) * mm});
            skPoint(sketch, "E17.34.1", {"position": v(2.7, 8.58) * mm});
            skPoint(sketch, "E17.34.2", {"position": v(3.62, 8.8) * mm});
            skPoint(sketch, "E17.34.3", {"position": v(2.89, 9.08) * mm});
            skPoint(sketch, "E17.34.4", {"position": v(3.7, 9.35) * mm});
            skPoint(sketch, "E17.34.5", {"position": v(3.44, 8.31) * mm});
            skArc(sketch, "E17.34.6", {"start": v(3.44, 8.31) * mm, "mid": v(3.62, 8.82) * mm, "end": v(3.7, 9.35) * mm});
            skArc(sketch, "E17.34.7", {"start": v(3.8, 8.15) * mm, "mid": v(3.62, 8.23) * mm, "end": v(3.44, 8.31) * mm});
            skArc(sketch, "E17.34.8", {"start": v(2.7, 8.58) * mm, "mid": v(2.9, 9.08) * mm, "end": v(3.18, 9.54) * mm});
            skArc(sketch, "E17.34.9", {"start": v(2.33, 8.69) * mm, "mid": v(2.52, 8.64) * mm, "end": v(2.7, 8.58) * mm});
            skArc(sketch, "E17.34.10", {"start": v(3.44, 9.45) * mm, "mid": v(3.57, 9.4) * mm, "end": v(3.7, 9.35) * mm});
            skArc(sketch, "E17.34.11", {"start": v(3.44, 9.45) * mm, "mid": v(3.3, 9.5) * mm, "end": v(3.18, 9.54) * mm});
            skPoint(sketch, "E17.35.0", {"position": v(1.48, 9.95) * mm});
            skPoint(sketch, "E17.35.1", {"position": v(1.17, 8.92) * mm});
            skPoint(sketch, "E17.35.2", {"position": v(2.04, 9.3) * mm});
            skPoint(sketch, "E17.35.3", {"position": v(1.27, 9.44) * mm});
            skPoint(sketch, "E17.35.4", {"position": v(2.02, 9.85) * mm});
            skPoint(sketch, "E17.35.5", {"position": v(1.95, 8.78) * mm});
            skArc(sketch, "E17.35.6", {"start": v(1.95, 8.78) * mm, "mid": v(2.04, 9.31) * mm, "end": v(2.02, 9.85) * mm});
            skArc(sketch, "E17.35.7", {"start": v(2.33, 8.69) * mm, "mid": v(2.14, 8.74) * mm, "end": v(1.95, 8.78) * mm});
            skArc(sketch, "E17.35.8", {"start": v(1.17, 8.92) * mm, "mid": v(1.27, 9.45) * mm, "end": v(1.48, 9.95) * mm});
            skArc(sketch, "E17.35.9", {"start": v(0.78, 8.96) * mm, "mid": v(0.98, 8.94) * mm, "end": v(1.17, 8.92) * mm});
            skArc(sketch, "E17.35.10", {"start": v(1.75, 9.9) * mm, "mid": v(1.88, 9.88) * mm, "end": v(2.02, 9.85) * mm});
            skArc(sketch, "E17.35.11", {"start": v(1.75, 9.9) * mm, "mid": v(1.61, 9.92) * mm, "end": v(1.48, 9.95) * mm});
            skSolve(sketch);
        }
        {
            var Q0;
            {var subQ52=sQuery(id+"F0.wireOp",EDGE,"E11.MirrorCS");Q0=makeQuery(id+"F0.imprint","IMPRINT",FACE,{"disambiguationData":[TD([[makeQuery(id+"F0.imprint","IMPRINT",EDGE,{"derivedFrom":subQ52}),-1.0]])]});}
            var Q1;
            {var subQ0=sQuery(id+"F0.wireOp",EDGE,"E8");Q1=makeQuery(id+"F0.imprint","IMPRINT",FACE,{"disambiguationData":[TD([[makeQuery(id+"F0.imprint","IMPRINT",EDGE,{"derivedFrom":subQ0}),1.0]])]});}
            extrude(context, id + "F1", {"entities" : qUnion([Q0, Q1]), "depth" : .1 * mm, "offsetDistance" : 25.4 * mm});
        }
    });
